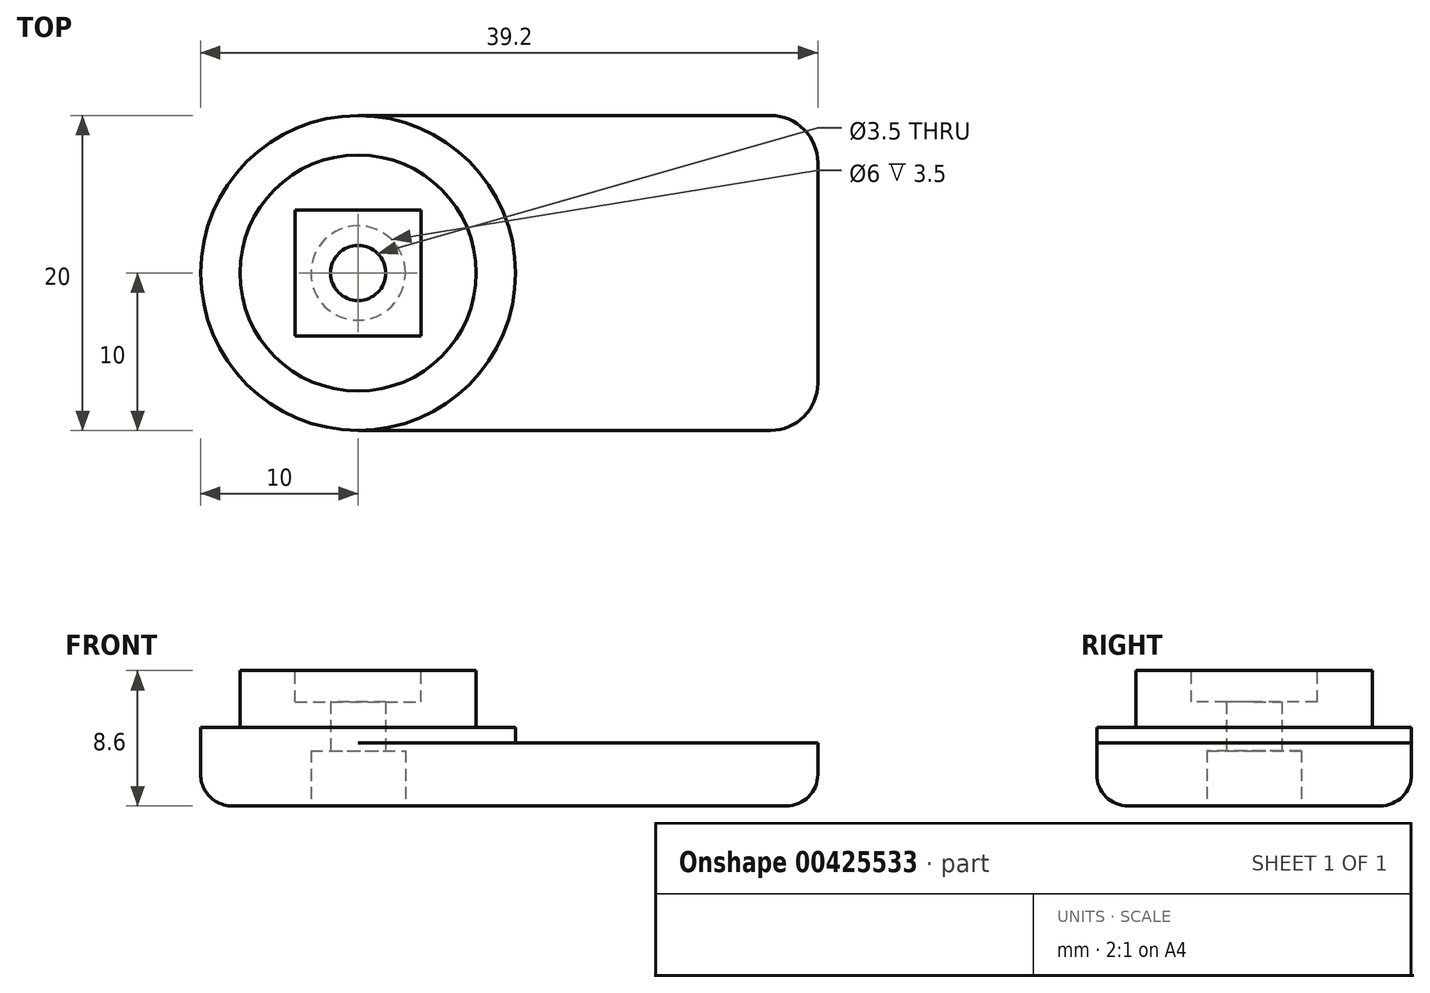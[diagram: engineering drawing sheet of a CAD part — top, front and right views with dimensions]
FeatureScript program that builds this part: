
annotation { "Feature Type Name" : "Feature", "Feature Type Description" : "" }
export const myFeature = defineFeature(function(context is Context, id is Id, definition is map)
    precondition{}
    {
        {
            var Q0;
            Q0=qCreatedBy(makeId("Top.planeOp"),FACE);
            var sketch = newSketch(context, id + "F0", { "sketchPlane" : qUnion([Q0])});
            skLineSegment(sketch, "E0.bottom", {"start": v(-10, 10) * mm, "end": v(29.2, 10) * mm});
            skLineSegment(sketch, "E0.top", {"start": v(-10, -10) * mm, "end": v(29.2, -10) * mm});
            skLineSegment(sketch, "E0.left", {"start": v(-10, 10) * mm, "end": v(-10, -10) * mm});
            skLineSegment(sketch, "E0.right", {"start": v(29.2, 10) * mm, "end": v(29.2, -10) * mm});
            skSolve(sketch);
        }
        {
            var Q0;
            Q0=qSketchRegion(id+"F0",true);
            extrude(context, id + "F1", {"entities" : qUnion([Q0]), "oppositeDirection" : true, "depth" : 4 * mm});
        }
        {
            var Q0;
            Q0=makeQuery(id+"F1.opExtrude","CAP_FACE",FACE,{"disambiguationData":[OSD([sQuery(id+"F0.wireOp",EDGE,"E0.bottom"),sQuery(id+"F0.wireOp",EDGE,"E0.top"),sQuery(id+"F0.wireOp",EDGE,"E0.left"),sQuery(id+"F0.wireOp",EDGE,"E0.right")])],"isStart":true});
            var sketch = newSketch(context, id + "F2", { "sketchPlane" : qUnion([Q0])});
            skCircle(sketch, "E1", {"center": v(0, 0) * mm, "radius": 7.5 * mm});
            skSolve(sketch);
        }
        {
            var Q0;
            Q0=qSketchRegion(id+"F2",true);
            extrude(context, id + "F3", {"entities" : qUnion([Q0]), "operationType" : NewBodyOperationType.ADD, "depth" : 4.6 * mm});
        }
        {
            var Q0;
            Q0=makeQuery(id+"F1.opExtrude","SWEPT_EDGE",EDGE,{"disambiguationData":[OSD([sQuery(id+"F0.wireOp",EDGE,"E0.top"),sQuery(id+"F0.wireOp",EDGE,"E0.left")])]});
            var Q1;
            Q1=makeQuery(id+"F1.opExtrude","SWEPT_EDGE",EDGE,{"disambiguationData":[OSD([sQuery(id+"F0.wireOp",EDGE,"E0.bottom"),sQuery(id+"F0.wireOp",EDGE,"E0.left")])]});
            fillet(context, id + "F4", {"entities" : qUnion([Q0, Q1]), "radius" : 10 * mm, "tangentPropagation" : true, "allowEdgeOverflow" : false});
        }
        {
            var Q0;
            Q0=makeQuery(id+"F1.opExtrude","CAP_FACE",FACE,{"disambiguationData":[OSD([sQuery(id+"F0.wireOp",EDGE,"E0.bottom"),sQuery(id+"F0.wireOp",EDGE,"E0.top"),sQuery(id+"F0.wireOp",EDGE,"E0.left"),sQuery(id+"F0.wireOp",EDGE,"E0.right")])],"isStart":true});
            var sketch = newSketch(context, id + "F5", { "sketchPlane" : qUnion([Q0])});
            skLineSegment(sketch, "E2.bottom", {"start": v(-10, 10) * mm, "end": v(7.5, 10) * mm});
            skLineSegment(sketch, "E2.top", {"start": v(-10, -10) * mm, "end": v(7.5, -10) * mm});
            skLineSegment(sketch, "E2.left", {"start": v(-10, 10) * mm, "end": v(-10, -10) * mm});
            skLineSegment(sketch, "E2.right", {"start": v(7.5, 10) * mm, "end": v(7.5, -10) * mm});
            skSolve(sketch);
        }
        {
            var Q0;
            Q0=qSketchRegion(id+"F5",true);
            extrude(context, id + "F6", {"entities" : qUnion([Q0]), "operationType" : NewBodyOperationType.ADD, "oppositeDirection" : true, "depth" : .5 * mm});
        }
        {
            var Q0;
            Q0=makeQuery(id+"F6.opExtrude","SWEPT_EDGE",EDGE,{"disambiguationData":[OSD([sQuery(id+"F5.wireOp",EDGE,"E2.top"),sQuery(id+"F5.wireOp",EDGE,"E2.left")])]});
            var Q1;
            Q1=makeQuery(id+"F6.opExtrude","SWEPT_EDGE",EDGE,{"disambiguationData":[OSD([sQuery(id+"F5.wireOp",EDGE,"E2.bottom"),sQuery(id+"F5.wireOp",EDGE,"E2.left")])]});
            fillet(context, id + "F7", {"entities" : qUnion([Q0, Q1]), "radius" : 10 * mm, "tangentPropagation" : true, "allowEdgeOverflow" : false});
        }
        {
            var Q0;
            Q0=makeQuery(id+"F3.opExtrude","CAP_FACE",FACE,{"disambiguationData":[OSD([sQuery(id+"F2.wireOp",EDGE,"E1")])],"isStart":false});
            var sketch = newSketch(context, id + "F8", { "sketchPlane" : qUnion([Q0])});
            skLineSegment(sketch, "E3.bottom", {"start": v(-4, 4) * mm, "end": v(4, 4) * mm});
            skLineSegment(sketch, "E3.top", {"start": v(-4, -4) * mm, "end": v(4, -4) * mm});
            skLineSegment(sketch, "E3.left", {"start": v(-4, 4) * mm, "end": v(-4, -4) * mm});
            skLineSegment(sketch, "E3.right", {"start": v(4, 4) * mm, "end": v(4, -4) * mm});
            skSolve(sketch);
        }
        {
            var Q0;
            Q0=qSketchRegion(id+"F8",true);
            extrude(context, id + "F9", {"entities" : qUnion([Q0]), "operationType" : NewBodyOperationType.REMOVE, "oppositeDirection" : true, "depth" : 2 * mm});
        }
        {
            var Q0;
            Q0=makeQuery(id+"F1.opExtrude","CAP_FACE",FACE,{"disambiguationData":[OSD([sQuery(id+"F0.wireOp",EDGE,"E0.bottom"),sQuery(id+"F0.wireOp",EDGE,"E0.top"),sQuery(id+"F0.wireOp",EDGE,"E0.left"),sQuery(id+"F0.wireOp",EDGE,"E0.right")])],"isStart":false});
            var sketch = newSketch(context, id + "F10", { "sketchPlane" : qUnion([Q0])});
            skPoint(sketch, "E4", {"position": v(0, 0) * mm});
            skSolve(sketch);
        }
        {
            var Q0;
            Q0=sQuery(id+"F10.wireOp",VERTEX,"E4");
            var Q1;
            Q1=makeQuery(id+"F1.opExtrude","SWEPT_BODY",BODY,{"disambiguationData":[OSD([sQuery(id+"F0.wireOp",EDGE,"E0.bottom"),sQuery(id+"F0.wireOp",EDGE,"E0.top"),sQuery(id+"F0.wireOp",EDGE,"E0.left"),sQuery(id+"F0.wireOp",EDGE,"E0.right")])]});
            hole(context, id + "F11", {"style" : HoleStyle.C_BORE, "endStyle" : HoleEndStyle.BLIND, "holeDiameter" : 3.5 * mm, "cBoreDiameter" : 6 * mm, "cBoreDepth" : 3.5 * mm, "holeDepth" : 10 * mm, "isTappedThrough" : true, "tappedDepth" : 12 * mm, "tapClearance" : 3, "startFromSketch" : true, "locations" : qUnion([Q0]), "scope" : qUnion([Q1])});
        }
        {
            var Q0;
            Q0=makeQuery(id+"F1.opExtrude","CAP_EDGE",EDGE,{"disambiguationData":[OSD([sQuery(id+"F0.wireOp",EDGE,"E0.bottom")])],"isStart":false});
            var Q1;
            Q1=makeQuery(id+"F1.opExtrude","CAP_EDGE",EDGE,{"disambiguationData":[OSD([sQuery(id+"F0.wireOp",EDGE,"E0.right")])],"isStart":false});
            fillet(context, id + "F12", {"entities" : qUnion([Q0, Q1]), "radius" : 2 * mm, "tangentPropagation" : true, "allowEdgeOverflow" : false});
        }
        {
            var Q0;
            Q0=makeQuery(id+"F1.opExtrude","SWEPT_EDGE",EDGE,{"disambiguationData":[OSD([sQuery(id+"F0.wireOp",EDGE,"E0.top"),sQuery(id+"F0.wireOp",EDGE,"E0.right")])]});
            var Q1;
            Q1=makeQuery(id+"F1.opExtrude","SWEPT_EDGE",EDGE,{"disambiguationData":[OSD([sQuery(id+"F0.wireOp",EDGE,"E0.bottom"),sQuery(id+"F0.wireOp",EDGE,"E0.right")])]});
            fillet(context, id + "F13", {"entities" : qUnion([Q0, Q1]), "radius" : 3 * mm, "tangentPropagation" : true, "allowEdgeOverflow" : false});
        }
        {
            var Q0;
            Q0=makeQuery(id+"F6.boolean.opBoolean","MERGE",FACE,{"derivedFrom":[makeQuery(id+"F1.opExtrude","CAP_FACE",FACE,{"disambiguationData":[OSD([sQuery(id+"F0.wireOp",EDGE,"E0.bottom"),sQuery(id+"F0.wireOp",EDGE,"E0.top"),sQuery(id+"F0.wireOp",EDGE,"E0.left"),sQuery(id+"F0.wireOp",EDGE,"E0.right")])],"isStart":true}),makeQuery(id+"F6.opExtrude","CAP_FACE",FACE,{"disambiguationData":[OSD([sQuery(id+"F5.wireOp",EDGE,"E2.bottom"),sQuery(id+"F5.wireOp",EDGE,"E2.top"),sQuery(id+"F5.wireOp",EDGE,"E2.left"),sQuery(id+"F5.wireOp",EDGE,"E2.right")])],"isStart":true})]});
            var sketch = newSketch(context, id + "F14", { "sketchPlane" : qUnion([Q0])});
            skCircle(sketch, "E5", {"center": v(0, 0) * mm, "radius": 10 * mm});
            skCircle(sketch, "E6", {"center": v(0, 0) * mm, "radius": 7.5 * mm});
            skSolve(sketch);
        }
        {
            var Q0;
            Q0 = qSketchRegion(id + "F14", true);
            extrude(context, id + "F15", {"entities" : qUnion([Q0]), "operationType" : NewBodyOperationType.ADD, "depth" : 1 * mm});
        }
    });
